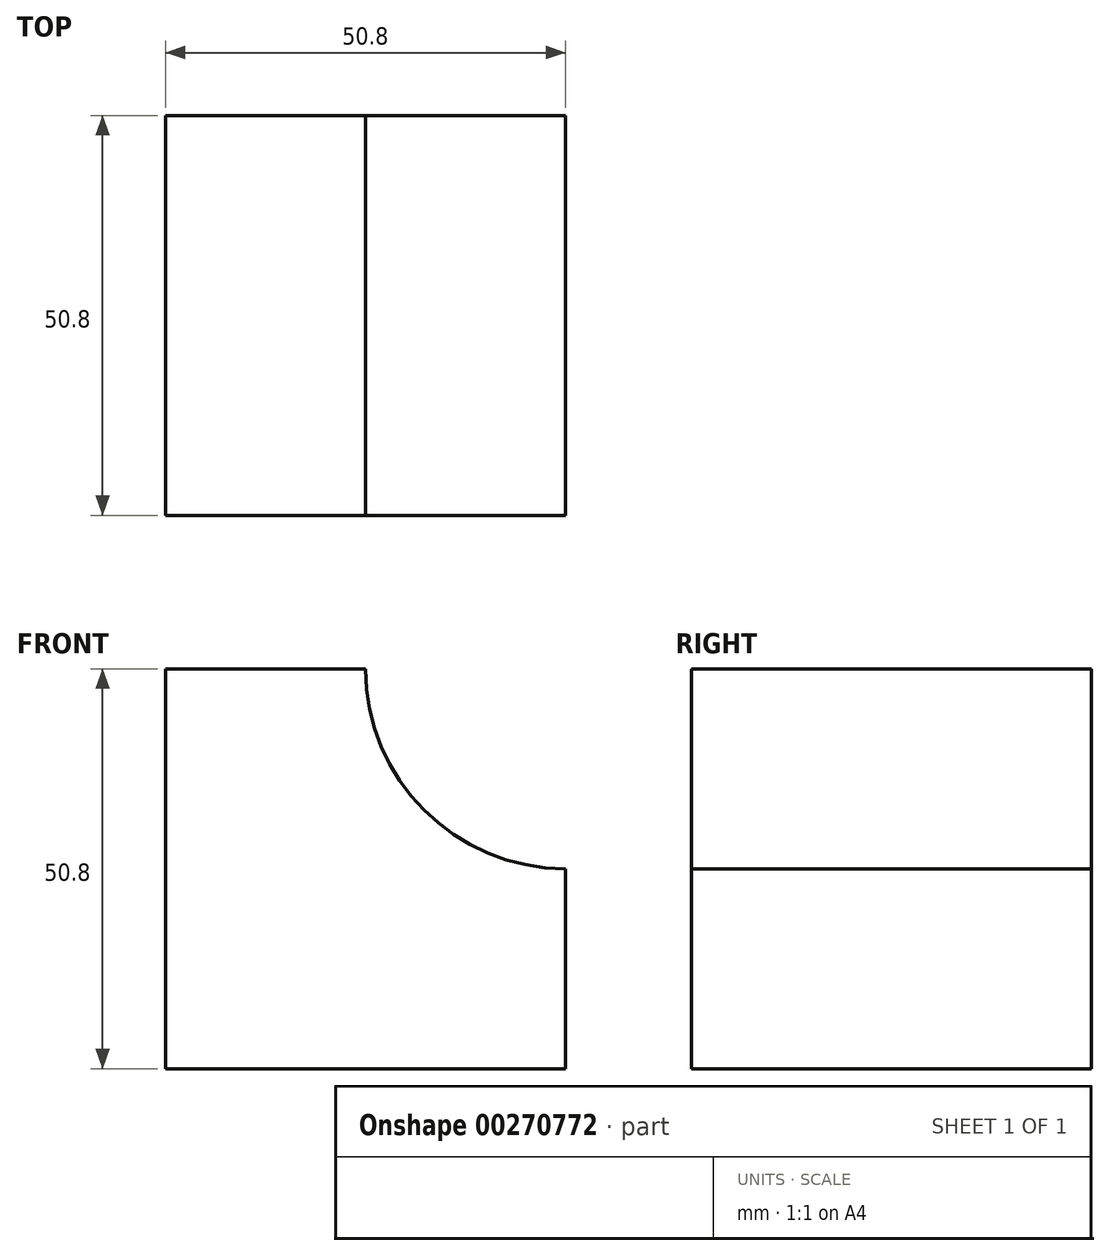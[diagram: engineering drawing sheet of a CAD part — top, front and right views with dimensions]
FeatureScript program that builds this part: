
annotation { "Feature Type Name" : "Feature", "Feature Type Description" : "" }
export const myFeature = defineFeature(function(context is Context, id is Id, definition is map)
    precondition{}
    {
        {
            var Q0;
            Q0=qCreatedBy(makeId("Front.planeOp"),FACE);
            var sketch = newSketch(context, id + "F0", { "sketchPlane" : qUnion([Q0])});
            skLineSegment(sketch, "E0", {"start": v(0, 0) * mm, "end": v(-50.8, 0) * mm});
            skLineSegment(sketch, "E1", {"start": v(-50.8, 0) * mm, "end": v(-50.8, 50.8) * mm});
            skLineSegment(sketch, "E2", {"start": v(-50.8, 50.8) * mm, "end": v(-25.4, 50.8) * mm});
            skLineSegment(sketch, "E3", {"start": v(0, 0) * mm, "end": v(0, 25.4) * mm});
            skArc(sketch, "E4", {"start": v(-25.4, 50.8) * mm, "mid": v(-17.96, 32.84) * mm, "end": v(0, 25.4) * mm});
            skSolve(sketch);
        }
        {
            var Q0;
            Q0 = qSketchRegion(id + "F0", true);
            extrude(context, id + "F1", {"entities" : qUnion([Q0]), "depth" : 50.8 * mm});
        }
    });
